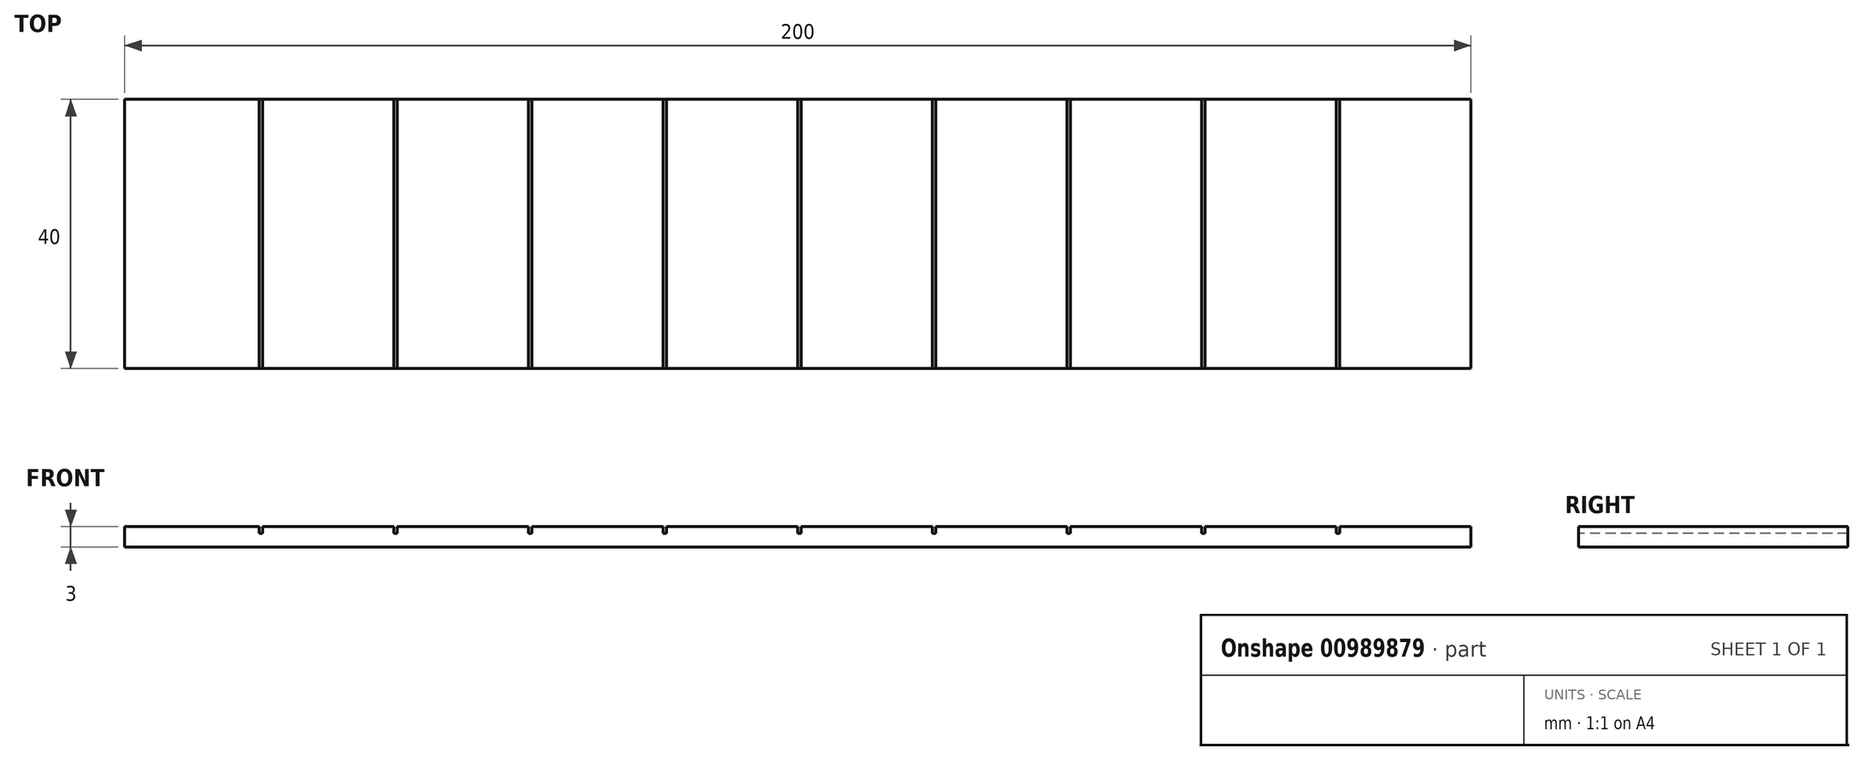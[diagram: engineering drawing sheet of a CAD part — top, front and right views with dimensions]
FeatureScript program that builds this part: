
annotation { "Feature Type Name" : "Feature", "Feature Type Description" : "" }
export const myFeature = defineFeature(function(context is Context, id is Id, definition is map)
    precondition{}
    {
        {
            var Q0;
            Q0=qCreatedBy(makeId("Top.planeOp"),FACE);
            var sketch = newSketch(context, id + "F0", { "sketchPlane" : qUnion([Q0])});
            skLineSegment(sketch, "E0.bottom", {"start": v(-59.67, 12.55) * mm, "end": v(140.33, 12.55) * mm});
            skLineSegment(sketch, "E0.top", {"start": v(-59.67, -27.45) * mm, "end": v(140.33, -27.45) * mm});
            skLineSegment(sketch, "E0.left", {"start": v(-59.67, 12.55) * mm, "end": v(-59.67, -27.45) * mm});
            skLineSegment(sketch, "E0.right", {"start": v(140.33, 12.55) * mm, "end": v(140.33, -27.45) * mm});
            skSolve(sketch);
        }
        {
            var Q0;
            Q0=makeQuery(id+"F0.imprint","IMPRINT",FACE,{"disambiguationData":[TD([[makeQuery(id+"F0.imprint","IMPRINT",EDGE,{"derivedFrom":sQuery(id+"F0.wireOp",EDGE,"E0.bottom")}),-1.0]])]});
            var sketch = newSketch(context, id + "F1", { "sketchPlane" : qUnion([Q0])});
            skLineSegment(sketch, "E1.bottom", {"start": v(-39.67, 12.55) * mm, "end": v(-39.17, 12.55) * mm});
            skLineSegment(sketch, "E1.top", {"start": v(-39.67, -28.45) * mm, "end": v(-39.17, -28.45) * mm});
            skLineSegment(sketch, "E1.left", {"start": v(-39.67, 12.55) * mm, "end": v(-39.67, -28.45) * mm});
            skLineSegment(sketch, "E1.right", {"start": v(-39.17, 12.55) * mm, "end": v(-39.17, -28.45) * mm});
            skLineSegment(sketch, "E2.bottom", {"start": v(-19.67, 13) * mm, "end": v(-19.17, 13) * mm});
            skLineSegment(sketch, "E2.top", {"start": v(-19.67, -28) * mm, "end": v(-19.17, -28) * mm});
            skLineSegment(sketch, "E2.left", {"start": v(-19.67, 13) * mm, "end": v(-19.67, -28) * mm});
            skLineSegment(sketch, "E2.right", {"start": v(-19.17, 13) * mm, "end": v(-19.17, -28) * mm});
            skLineSegment(sketch, "E3.bottom", {"start": v(0.33, 13.1) * mm, "end": v(0.83, 13.1) * mm});
            skLineSegment(sketch, "E3.top", {"start": v(0.33, -27.89) * mm, "end": v(0.83, -27.89) * mm});
            skLineSegment(sketch, "E3.left", {"start": v(0.33, 13.1) * mm, "end": v(0.33, -27.89) * mm});
            skLineSegment(sketch, "E3.right", {"start": v(0.83, 13.1) * mm, "end": v(0.83, -27.89) * mm});
            skLineSegment(sketch, "E4.bottom", {"start": v(20.33, 13.14) * mm, "end": v(20.83, 13.14) * mm});
            skLineSegment(sketch, "E4.top", {"start": v(20.33, -27.86) * mm, "end": v(20.83, -27.86) * mm});
            skLineSegment(sketch, "E4.left", {"start": v(20.33, 13.14) * mm, "end": v(20.33, -27.86) * mm});
            skLineSegment(sketch, "E4.right", {"start": v(20.83, 13.14) * mm, "end": v(20.83, -27.86) * mm});
            skLineSegment(sketch, "E5.bottom", {"start": v(40.33, 12.55) * mm, "end": v(40.83, 12.55) * mm});
            skLineSegment(sketch, "E5.top", {"start": v(40.33, -28.45) * mm, "end": v(40.83, -28.45) * mm});
            skLineSegment(sketch, "E5.left", {"start": v(40.33, 12.55) * mm, "end": v(40.33, -28.45) * mm});
            skLineSegment(sketch, "E5.right", {"start": v(40.83, 12.55) * mm, "end": v(40.83, -28.45) * mm});
            skLineSegment(sketch, "E6.bottom", {"start": v(60.33, 13.11) * mm, "end": v(60.83, 13.11) * mm});
            skLineSegment(sketch, "E6.top", {"start": v(60.33, -27.88) * mm, "end": v(60.83, -27.88) * mm});
            skLineSegment(sketch, "E6.left", {"start": v(60.33, 13.11) * mm, "end": v(60.33, -27.88) * mm});
            skLineSegment(sketch, "E6.right", {"start": v(60.83, 13.11) * mm, "end": v(60.83, -27.88) * mm});
            skLineSegment(sketch, "E7.bottom", {"start": v(80.33, 12.8) * mm, "end": v(80.83, 12.8) * mm});
            skLineSegment(sketch, "E7.top", {"start": v(80.33, -28.2) * mm, "end": v(80.83, -28.2) * mm});
            skLineSegment(sketch, "E7.left", {"start": v(80.33, 12.8) * mm, "end": v(80.33, -28.2) * mm});
            skLineSegment(sketch, "E7.right", {"start": v(80.83, 12.8) * mm, "end": v(80.83, -28.2) * mm});
            skLineSegment(sketch, "E8.bottom", {"start": v(100.33, 13.16) * mm, "end": v(100.83, 13.16) * mm});
            skLineSegment(sketch, "E8.top", {"start": v(100.33, -27.83) * mm, "end": v(100.83, -27.83) * mm});
            skLineSegment(sketch, "E8.left", {"start": v(100.33, 13.16) * mm, "end": v(100.33, -27.83) * mm});
            skLineSegment(sketch, "E8.right", {"start": v(100.83, 13.16) * mm, "end": v(100.83, -27.83) * mm});
            skLineSegment(sketch, "E9.bottom", {"start": v(120.33, 13.1) * mm, "end": v(120.83, 13.1) * mm});
            skLineSegment(sketch, "E9.top", {"start": v(120.33, -27.89) * mm, "end": v(120.83, -27.89) * mm});
            skLineSegment(sketch, "E9.left", {"start": v(120.33, 13.1) * mm, "end": v(120.33, -27.89) * mm});
            skLineSegment(sketch, "E9.right", {"start": v(120.83, 13.1) * mm, "end": v(120.83, -27.89) * mm});
            skSolve(sketch);
        }
        {
            var Q0;
            Q0=makeQuery(id+"F0.imprint","IMPRINT",FACE,{"disambiguationData":[TD([[makeQuery(id+"F0.imprint","IMPRINT",EDGE,{"derivedFrom":sQuery(id+"F0.wireOp",EDGE,"E0.bottom")}),-1.0]])]});
            extrude(context, id + "F2", {"entities" : qUnion([Q0]), "oppositeDirection" : true, "depth" : 3 * mm, "offsetDistance" : 25 * mm});
        }
        {
            var Q0;
            {var subQ0=sQuery(id+"F1.wireOp",EDGE,"E1.bottom");Q0=makeQuery(id+"F1.imprint","IMPRINT",FACE,{"disambiguationData":[TD([[makeQuery(id+"F1.imprint","IMPRINT",EDGE,{"derivedFrom":subQ0}),-1.0]])]});}
            var Q1;
            {var subQ0=sQuery(id+"F1.wireOp",EDGE,"E2.left");var subQ1=makeQuery(id+"F0.imprint","IMPRINT",EDGE,{"derivedFrom":sQuery(id+"F0.wireOp",EDGE,"E0.bottom")});var subQ2=makeQuery(id+"F1.imprint","INTERSECT",VERTEX,{"derivedFrom":[subQ1,subQ0]});Q1=makeQuery(id+"F1.imprint","IMPRINT",FACE,{"disambiguationData":[TD([[makeQuery(id+"F1.imprint","IMPRINT",EDGE,{"disambiguationData":[TD([[subQ2,-1.0]])],"derivedFrom":subQ0}),1.0]])]});}
            var Q2;
            {var subQ0=sQuery(id+"F1.wireOp",EDGE,"E3.left");var subQ1=makeQuery(id+"F0.imprint","IMPRINT",EDGE,{"derivedFrom":sQuery(id+"F0.wireOp",EDGE,"E0.bottom")});var subQ2=makeQuery(id+"F1.imprint","INTERSECT",VERTEX,{"derivedFrom":[subQ1,subQ0]});Q2=makeQuery(id+"F1.imprint","IMPRINT",FACE,{"disambiguationData":[TD([[makeQuery(id+"F1.imprint","IMPRINT",EDGE,{"disambiguationData":[TD([[subQ2,-1.0]])],"derivedFrom":subQ0}),1.0]])]});}
            var Q3;
            {var subQ0=sQuery(id+"F1.wireOp",EDGE,"E4.left");var subQ1=makeQuery(id+"F0.imprint","IMPRINT",EDGE,{"derivedFrom":sQuery(id+"F0.wireOp",EDGE,"E0.bottom")});var subQ2=makeQuery(id+"F1.imprint","INTERSECT",VERTEX,{"derivedFrom":[subQ1,subQ0]});Q3=makeQuery(id+"F1.imprint","IMPRINT",FACE,{"disambiguationData":[TD([[makeQuery(id+"F1.imprint","IMPRINT",EDGE,{"disambiguationData":[TD([[subQ2,-1.0]])],"derivedFrom":subQ0}),1.0]])]});}
            var Q4;
            {var subQ0=sQuery(id+"F1.wireOp",EDGE,"E5.bottom");Q4=makeQuery(id+"F1.imprint","IMPRINT",FACE,{"disambiguationData":[TD([[makeQuery(id+"F1.imprint","IMPRINT",EDGE,{"derivedFrom":subQ0}),-1.0]])]});}
            var Q5;
            {var subQ0=sQuery(id+"F1.wireOp",EDGE,"E6.left");var subQ1=makeQuery(id+"F0.imprint","IMPRINT",EDGE,{"derivedFrom":sQuery(id+"F0.wireOp",EDGE,"E0.bottom")});var subQ2=makeQuery(id+"F1.imprint","INTERSECT",VERTEX,{"derivedFrom":[subQ1,subQ0]});Q5=makeQuery(id+"F1.imprint","IMPRINT",FACE,{"disambiguationData":[TD([[makeQuery(id+"F1.imprint","IMPRINT",EDGE,{"disambiguationData":[TD([[subQ2,-1.0]])],"derivedFrom":subQ0}),1.0]])]});}
            var Q6;
            {var subQ0=sQuery(id+"F1.wireOp",EDGE,"E7.left");var subQ1=makeQuery(id+"F0.imprint","IMPRINT",EDGE,{"derivedFrom":sQuery(id+"F0.wireOp",EDGE,"E0.bottom")});var subQ2=makeQuery(id+"F1.imprint","INTERSECT",VERTEX,{"derivedFrom":[subQ1,subQ0]});Q6=makeQuery(id+"F1.imprint","IMPRINT",FACE,{"disambiguationData":[TD([[makeQuery(id+"F1.imprint","IMPRINT",EDGE,{"disambiguationData":[TD([[subQ2,-1.0]])],"derivedFrom":subQ0}),1.0]])]});}
            var Q7;
            {var subQ0=sQuery(id+"F1.wireOp",EDGE,"E8.left");var subQ1=makeQuery(id+"F0.imprint","IMPRINT",EDGE,{"derivedFrom":sQuery(id+"F0.wireOp",EDGE,"E0.bottom")});var subQ2=makeQuery(id+"F1.imprint","INTERSECT",VERTEX,{"derivedFrom":[subQ1,subQ0]});Q7=makeQuery(id+"F1.imprint","IMPRINT",FACE,{"disambiguationData":[TD([[makeQuery(id+"F1.imprint","IMPRINT",EDGE,{"disambiguationData":[TD([[subQ2,-1.0]])],"derivedFrom":subQ0}),1.0]])]});}
            var Q8;
            {var subQ0=sQuery(id+"F1.wireOp",EDGE,"E9.left");var subQ1=makeQuery(id+"F0.imprint","IMPRINT",EDGE,{"derivedFrom":sQuery(id+"F0.wireOp",EDGE,"E0.bottom")});var subQ2=makeQuery(id+"F1.imprint","INTERSECT",VERTEX,{"derivedFrom":[subQ1,subQ0]});Q8=makeQuery(id+"F1.imprint","IMPRINT",FACE,{"disambiguationData":[TD([[makeQuery(id+"F1.imprint","IMPRINT",EDGE,{"disambiguationData":[TD([[subQ2,-1.0]])],"derivedFrom":subQ0}),1.0]])]});}
            extrude(context, id + "F3", {"entities" : qUnion([Q0, Q1, Q2, Q3, Q4, Q5, Q6, Q7, Q8]), "operationType" : NewBodyOperationType.REMOVE, "oppositeDirection" : true, "depth" : 1 * mm, "offsetDistance" : 25 * mm});
        }
    });
